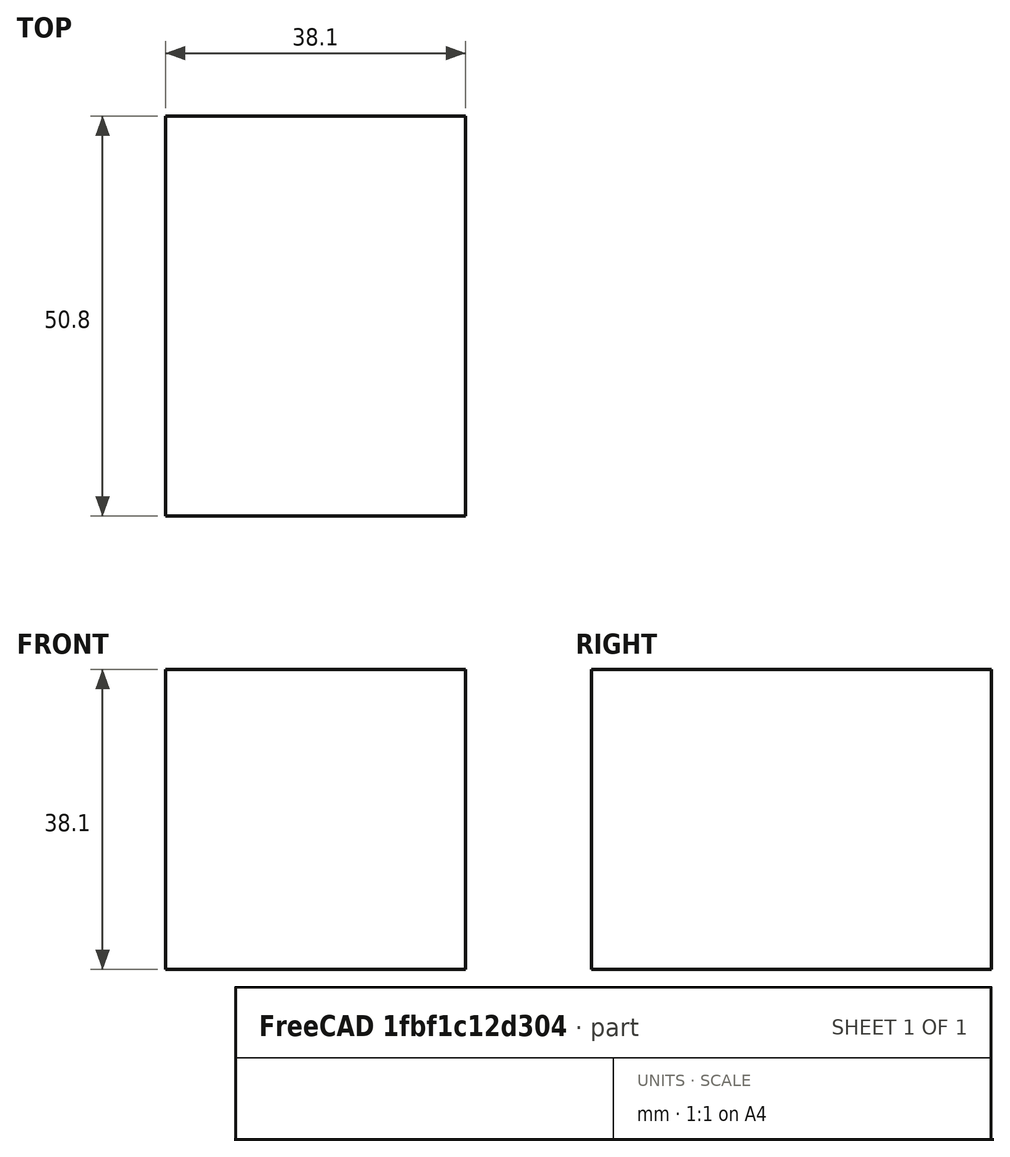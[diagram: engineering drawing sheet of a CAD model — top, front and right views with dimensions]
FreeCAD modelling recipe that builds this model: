
FCSTD DOCUMENT  (FreeCAD 0.19R24291 (Git))
Label: topblock
License: All rights reserved
LicenseURL: http://en.wikipedia.org/wiki/All_rights_reserved
objects: Sketcher::SketchObject×1, PartDesign::Pad×1, PartDesign::Body×1
note: 4 computed .brp shape members not serialized (recipe doc carries the construction recipe); baked Part::Feature solids carry a one-line shape summary decoded from their .brp

FEATURE [Sketcher::SketchObject] Sketch
  FullyConstrained = false
  MapMode = 5
  Placement = pos=(0,0,0) rot=(0.57735,0.57735,0.57735;2.0944rad)
  Support = -> [YZ_Plane]
  sketch-geometry (4):
    g0: LineSegment StartX=0 StartY=0 StartZ=0 EndX=50.8 EndY=0 EndZ=0
    g1: LineSegment StartX=50.8 StartY=0 StartZ=0 EndX=50.8 EndY=38.1 EndZ=0
    g2: LineSegment StartX=50.8 StartY=38.1 StartZ=0 EndX=0 EndY=38.1 EndZ=0
    g3: LineSegment StartX=0 StartY=38.1 StartZ=0 EndX=0 EndY=0 EndZ=0
  constraints (9):
    c: Coincident(g0,g1)
    c: Coincident(g1,g2)
    c: Coincident(g2,g3)
    c: Coincident(g3,g0)
    c: Horizontal(g0)
    c: Horizontal(g2)
    c: Vertical(g1)
    c: Vertical(g3)
    c: Coincident(g0,g-1)
FEATURE [PartDesign::Pad] Pad
  Direction = (1,1,1)
  Length = 38.1
  Length2 = 99.9998
  Placement = pos=(0,0,0) rot=(0.57735,0.57735,0.57735;2.0944rad)
  Profile = -> Sketch
  Refine = true
  Type = 0
FEATURE [PartDesign::Body] Body
  Group = -> [Sketch,Pad]
  Origin = -> Origin
  Tip = -> Pad
